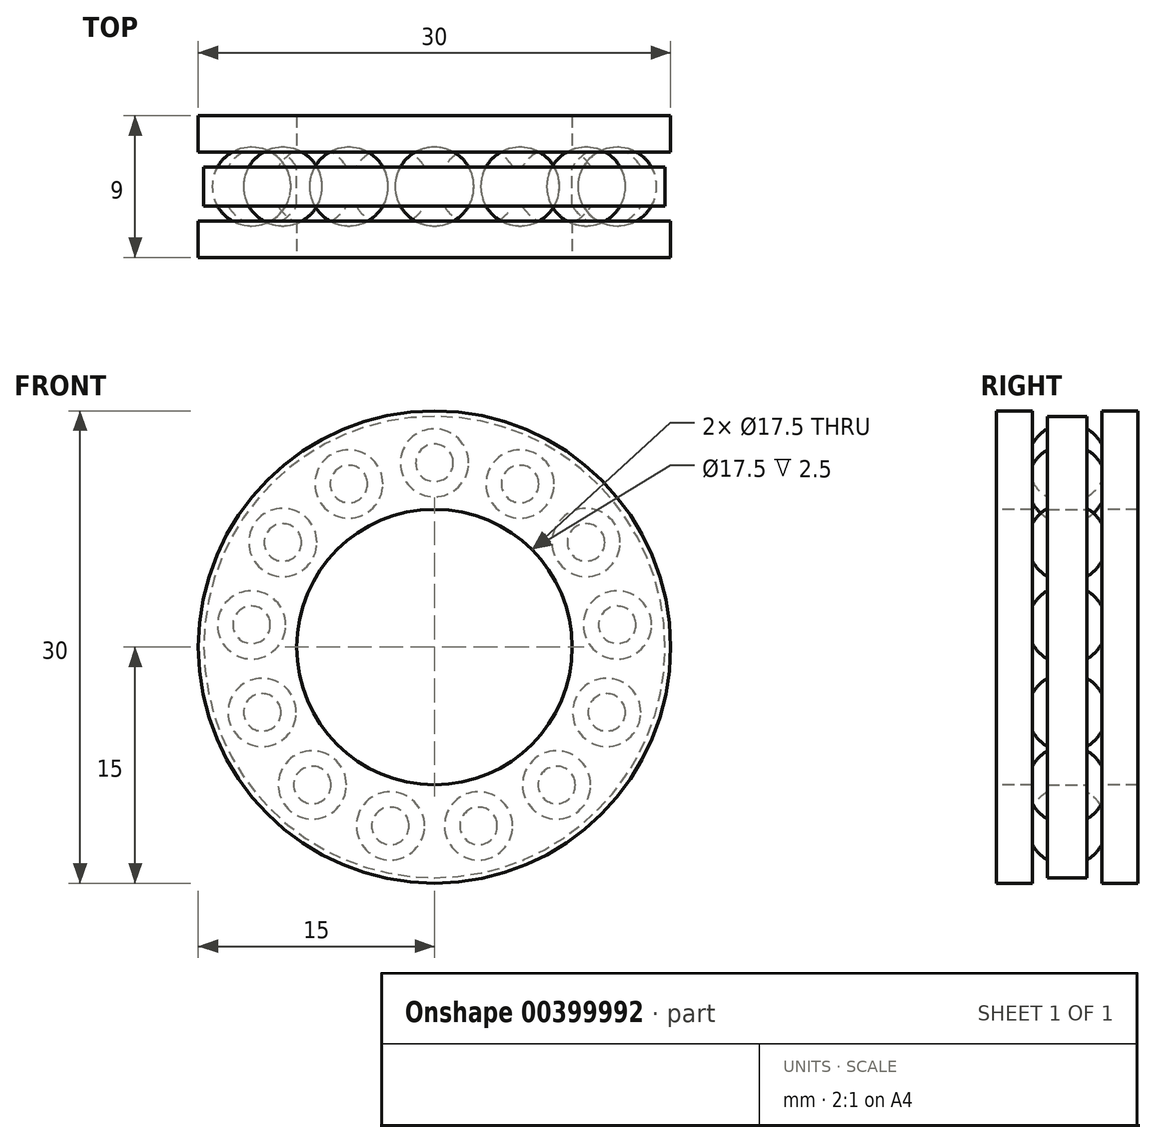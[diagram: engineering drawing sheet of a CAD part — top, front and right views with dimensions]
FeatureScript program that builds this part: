
annotation { "Feature Type Name" : "Feature", "Feature Type Description" : "" }
export const myFeature = defineFeature(function(context is Context, id is Id, definition is map)
    precondition{}
    {
        {
            var Q0;
            Q0=qCreatedBy(makeId("Front.planeOp"),FACE);
            var sketch = newSketch(context, id + "F0", { "sketchPlane" : qUnion([Q0])});
            skCircle(sketch, "E0", {"center": v(0, 0) * mm, "radius": 8.75 * mm});
            skCircle(sketch, "E1", {"center": v(0, 0) * mm, "radius": 14.65 * mm});
            skSolve(sketch);
        }
        {
            var Q0;
            Q0 = qSketchRegion(id + "F0", true);
            extrude(context, id + "F1", {"entities" : qUnion([Q0]), "depth" : 2.5 * mm, "symmetric" : true});
        }
        {
            var Q0;
            Q0=qCreatedBy(makeId("Front.planeOp"),FACE);
            var sketch = newSketch(context, id + "F2", { "sketchPlane" : qUnion([Q0])});
            skArc(sketch, "E2", {"start": v(0, 9.2) * mm, "mid": v(2.5, 11.7) * mm, "end": v(0, 14.2) * mm});
            skLineSegment(sketch, "E3", {"start": v(0, 14.2) * mm, "end": v(0, 9.2) * mm});
            skLineSegment(sketch, "E4", {"start": v(0, 11.7) * mm, "end": v(2.5, 11.7) * mm, "construction": true});
            skLineSegment(sketch, "E5", {"start": v(0, 8.75) * mm, "end": v(0, 14.65) * mm, "construction": true});
            skSolve(sketch);
        }
        {
            var Q0;
            Q0 = qSketchRegion(id + "F2", true);
            var Q1;
            Q1=sQuery(id+"F2.wireOp",EDGE,"E3");
            revolve(context, id + "F3", {"operationType" : NewBodyOperationType.ADD, "entities" : qUnion([Q0]), "axis" : qUnion([Q1]), "revolveType" : RevolveType.FULL});
        }
        {
            var Q0;
            Q0=makeQuery(id+"F1.opExtrude","SWEPT_BODY",BODY,{"disambiguationData":[OSD([sQuery(id+"F0.wireOp",EDGE,"E0"),sQuery(id+"F0.wireOp",EDGE,"E1")])]});
            var Q1;
            Q1=makeQuery(id+"F1.opExtrude","CAP_EDGE",EDGE,{"disambiguationData":[OSD([sQuery(id+"F0.wireOp",EDGE,"E1")])],"isStart":false});
            circularPattern(context, id + "F4", {"operationType" : NewBodyOperationType.ADD, "entities" : qUnion([Q0]), "axis" : qUnion([Q1]), "angle" : 360 * degree, "instanceCount" : 13, "equalSpace" : true, "computeTransformsWithoutBuiltin" : true});
        }
        {
            var Q0;
            Q0=qCreatedBy(makeId("Right.planeOp"),FACE);
            var sketch = newSketch(context, id + "F5", { "sketchPlane" : qUnion([Q0])});
            skLineSegment(sketch, "E6", {"start": v(2.2, 15) * mm, "end": v(4.5, 15) * mm});
            skLineSegment(sketch, "E7", {"start": v(4.5, 15) * mm, "end": v(4.5, 8.75) * mm});
            skLineSegment(sketch, "E8", {"start": v(0, 11.7) * mm, "end": v(0, 0) * mm, "construction": true});
            skLineSegment(sketch, "E9", {"start": v(2.2, 8.75) * mm, "end": v(4.5, 8.75) * mm});
            skLineSegment(sketch, "E10", {"start": v(0, 0) * mm, "end": v(4.5, 0) * mm, "construction": true});
            skLineSegment(sketch, "E11.MirrorCS", {"start": v(-2.2, 15) * mm, "end": v(-4.5, 15) * mm});
            skLineSegment(sketch, "E12.MirrorCS", {"start": v(-4.5, 15) * mm, "end": v(-4.5, 8.75) * mm});
            skLineSegment(sketch, "E13.MirrorCS", {"start": v(-2.2, 8.75) * mm, "end": v(-4.5, 8.75) * mm});
            skPoint(sketch, "E14.MirrorCS.end.orphan", {"position": v(-2.2, 15) * mm});
            skPoint(sketch, "E15.MirrorCS.start.orphan", {"position": v(-2.2, 8.75) * mm});
            skLineSegment(sketch, "E16", {"start": v(2.2, 15) * mm, "end": v(2.2, 8.75) * mm});
            skLineSegment(sketch, "E17.MirrorCS", {"start": v(-2.2, 15) * mm, "end": v(-2.2, 8.75) * mm});
            skSolve(sketch);
        }
        {
            var Q0;
            Q0=makeQuery(id+"F5.imprint","IMPRINT",FACE,{"disambiguationData":[TD([[makeQuery(id+"F5.imprint","IMPRINT",EDGE,{"derivedFrom":sQuery(id+"F5.wireOp",EDGE,"E6")}),-1.0]])]});
            var Q1;
            Q1=makeQuery(id+"F5.imprint","IMPRINT",FACE,{"disambiguationData":[TD([[makeQuery(id+"F5.imprint","IMPRINT",EDGE,{"derivedFrom":sQuery(id+"F5.wireOp",EDGE,"E11.MirrorCS")}),1.0]])]});
            var Q2;
            Q2=sQuery(id+"F5.wireOp",EDGE,"E10");
            revolve(context, id + "F6", {"operationType" : NewBodyOperationType.ADD, "entities" : qUnion([Q0, Q1]), "axis" : qUnion([Q2]), "revolveType" : RevolveType.FULL});
        }
    });
